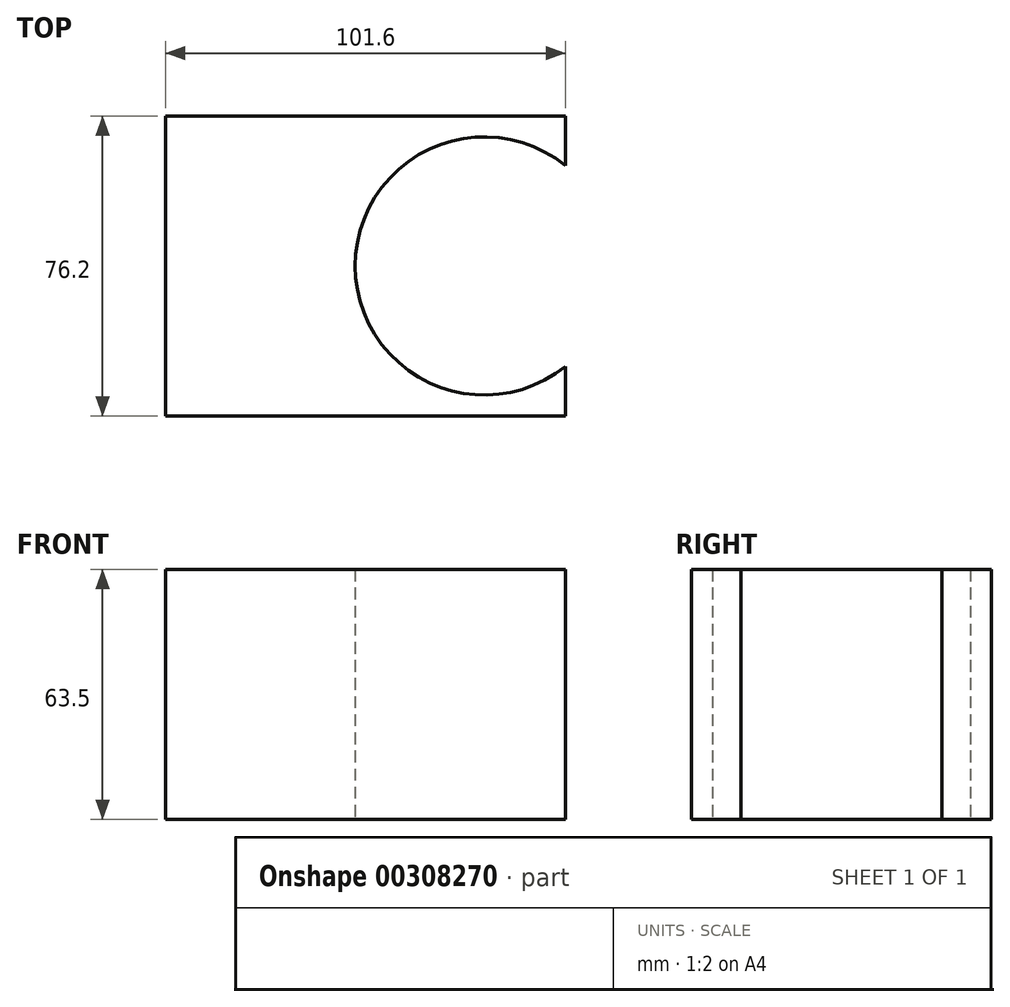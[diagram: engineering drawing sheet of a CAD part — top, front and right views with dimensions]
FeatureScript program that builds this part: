
annotation { "Feature Type Name" : "Feature", "Feature Type Description" : "" }
export const myFeature = defineFeature(function(context is Context, id is Id, definition is map)
    precondition{}
    {
        {
            var Q0;
            Q0=qCreatedBy(makeId("Front.planeOp"),FACE);
            var sketch = newSketch(context, id + "F0", { "sketchPlane" : qUnion([Q0])});
            skLineSegment(sketch, "E0", {"start": v(-43.6, -30.18) * mm, "end": v(58, -30.18) * mm});
            skLineSegment(sketch, "E1", {"start": v(58, -30.18) * mm, "end": v(58, 33.32) * mm});
            skLineSegment(sketch, "E2", {"start": v(58, 33.32) * mm, "end": v(-43.6, 33.32) * mm});
            skLineSegment(sketch, "E3", {"start": v(-43.6, 33.32) * mm, "end": v(-43.6, -30.18) * mm});
            skSolve(sketch);
        }
        {
            var Q0;
            Q0 = qSketchRegion(id + "F0", true);
            extrude(context, id + "F1", {"entities" : qUnion([Q0]), "depth" : 76.2 * mm});
        }
        {
            var Q0;
            Q0=qCreatedBy(makeId("Top.planeOp"),FACE);
            var sketch = newSketch(context, id + "F2", { "sketchPlane" : qUnion([Q0])});
            skCircle(sketch, "E4", {"center": v(37.37, -38.08) * mm, "radius": 32.8 * mm});
            skSolve(sketch);
        }
        {
            var Q0;
            Q0 = qSketchRegion(id + "F2", true);
            extrude(context, id + "F3", {"entities" : qUnion([Q0]), "operationType" : NewBodyOperationType.REMOVE, "depth" : 127 * mm});
        }
        {
            var Q0;
            Q0=makeQuery(id+"F3.boolean.opBoolean","COPY",FACE,{"derivedFrom":makeQuery(id+"F3.opExtrude","CAP_FACE",FACE,{"disambiguationData":[OSD([sQuery(id+"F2.wireOp",EDGE,"E4")])],"isStart":true})});
            extrude(context, id + "F4", {"entities" : qUnion([Q0]), "operationType" : NewBodyOperationType.REMOVE, "oppositeDirection" : true, "depth" : 127 * mm});
        }
    });
